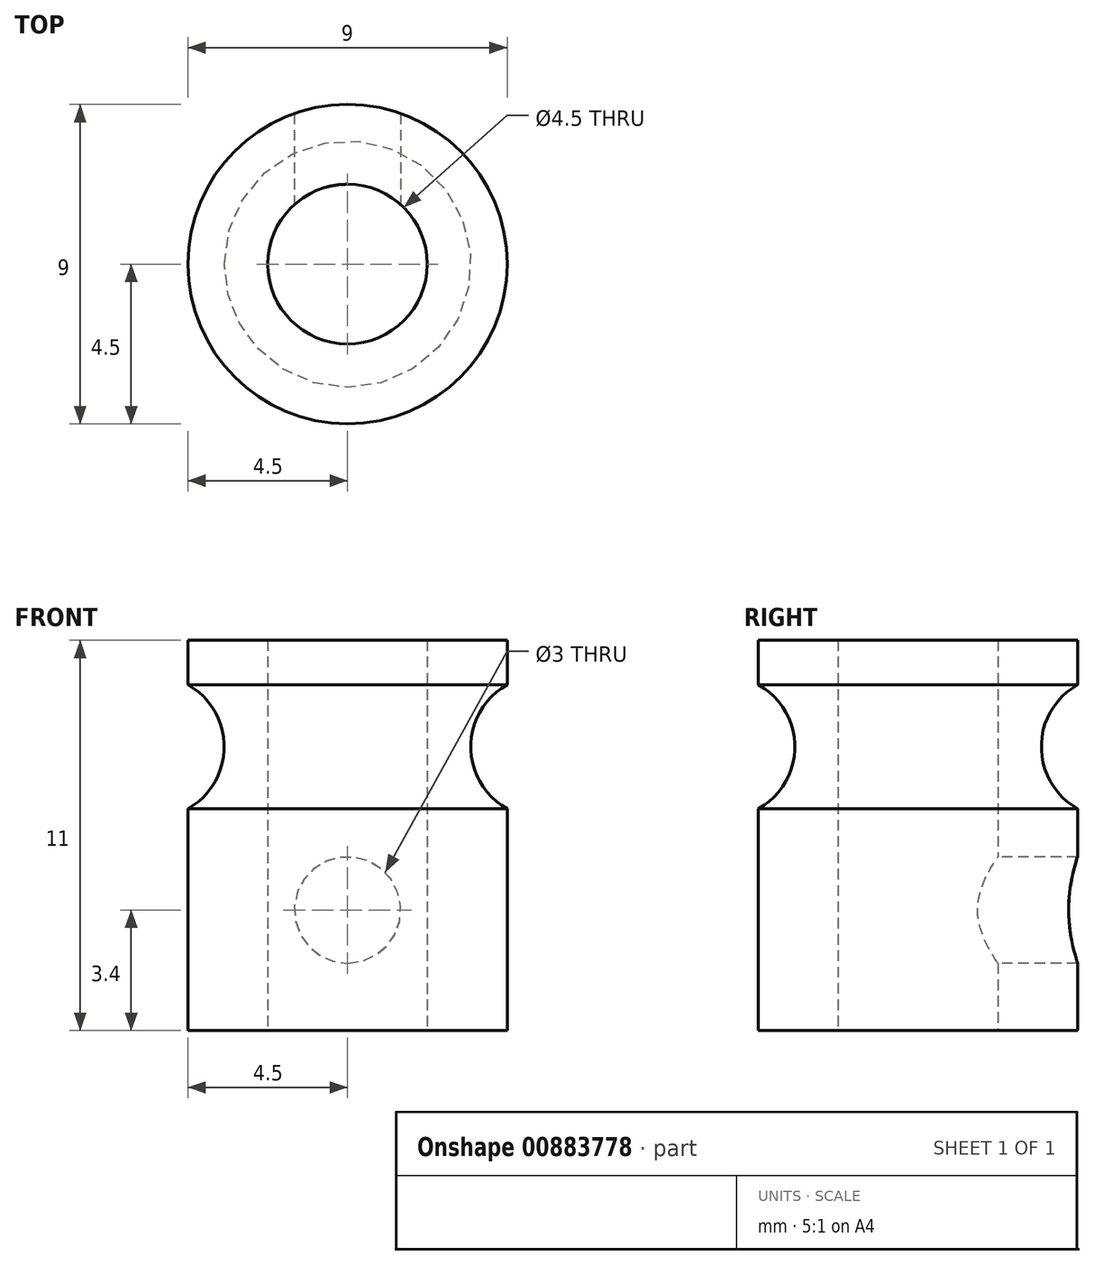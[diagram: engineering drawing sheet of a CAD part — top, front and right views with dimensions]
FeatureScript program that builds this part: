
annotation { "Feature Type Name" : "Feature", "Feature Type Description" : "" }
export const myFeature = defineFeature(function(context is Context, id is Id, definition is map)
    precondition{}
    {
        {
            var Q0;
            Q0=qCreatedBy(makeId("Top.planeOp"),FACE);
            var sketch = newSketch(context, id + "F0", { "sketchPlane" : qUnion([Q0])});
            skCircle(sketch, "E0", {"center": v(0, 0) * mm, "radius": 2.25 * mm});
            skCircle(sketch, "E1", {"center": v(0, 0) * mm, "radius": 4.5 * mm});
            skSolve(sketch);
        }
        {
            var Q0;
            Q0=makeQuery(id+"F0.imprint","IMPRINT",FACE,{"disambiguationData":[TD([[makeQuery(id+"F0.imprint","IMPRINT",EDGE,{"derivedFrom":sQuery(id+"F0.wireOp",EDGE,"E0")}),-1.0]])]});
            extrude(context, id + "F1", {"entities" : qUnion([Q0]), "depth" : 11 * mm, "offsetDistance" : 25 * mm});
        }
        {
            var Q0;
            Q0=qCreatedBy(makeId("Front.planeOp"),FACE);
            var sketch = newSketch(context, id + "F2", { "sketchPlane" : qUnion([Q0])});
            skLineSegment(sketch, "E2", {"start": v(-10.27, 6) * mm, "end": v(12.86, 6) * mm, "construction": true});
            skLineSegment(sketch, "E3", {"start": v(-10.27, 10) * mm, "end": v(12.75, 10) * mm, "construction": true});
            skLineSegment(sketch, "E4", {"start": v(-11.07, 3.4) * mm, "end": v(11.07, 3.4) * mm, "construction": true});
            skCircle(sketch, "E5", {"center": v(0, 3.4) * mm, "radius": 1.5 * mm});
            skCircle(sketch, "E6", {"center": v(0, 8) * mm, "radius": 3.48 * mm, "construction": true});
            skLineSegment(sketch, "E7", {"start": v(-3.47, 8.04) * mm, "end": v(-3.47, 4.36) * mm, "construction": true});
            skLineSegment(sketch, "E8", {"start": v(5.88, 8) * mm, "end": v(-5.88, 8) * mm, "construction": true});
            skLineSegment(sketch, "E9", {"start": v(0, 12.3) * mm, "end": v(0, 0.44) * mm, "construction": true});
            skCircle(sketch, "E10", {"center": v(-5.47, 8) * mm, "radius": 2 * mm});
            skSolve(sketch);
        }
        {
            var Q0;
            Q0=makeQuery(id+"F2.imprint","IMPRINT",FACE,{"disambiguationData":[TD([[makeQuery(id+"F2.imprint","IMPRINT",EDGE,{"derivedFrom":sQuery(id+"F2.wireOp",EDGE,"E5")}),1.0]])]});
            extrude(context, id + "F3", {"entities" : qUnion([Q0]), "operationType" : NewBodyOperationType.REMOVE, "endBound" : BoundingType.THROUGH_ALL, "oppositeDirection" : true, "depth" : 25 * mm, "offsetDistance" : 25 * mm});
        }
        {
            var Q0;
            Q0=makeQuery(id+"F2.imprint","IMPRINT",FACE,{"disambiguationData":[TD([[makeQuery(id+"F2.imprint","IMPRINT",EDGE,{"derivedFrom":sQuery(id+"F2.wireOp",EDGE,"E10")}),1.0]])]});
            var Q1;
            Q1=sQuery(id+"F2.wireOp",EDGE,"E9");
            revolve(context, id + "F4", {"operationType" : NewBodyOperationType.REMOVE, "surfaceOperationType" : NewSurfaceOperationType.NEW, "entities" : qUnion([Q0]), "axis" : qUnion([Q1]), "revolveType" : RevolveType.FULL, "oppositeDirection" : true});
        }
    });
